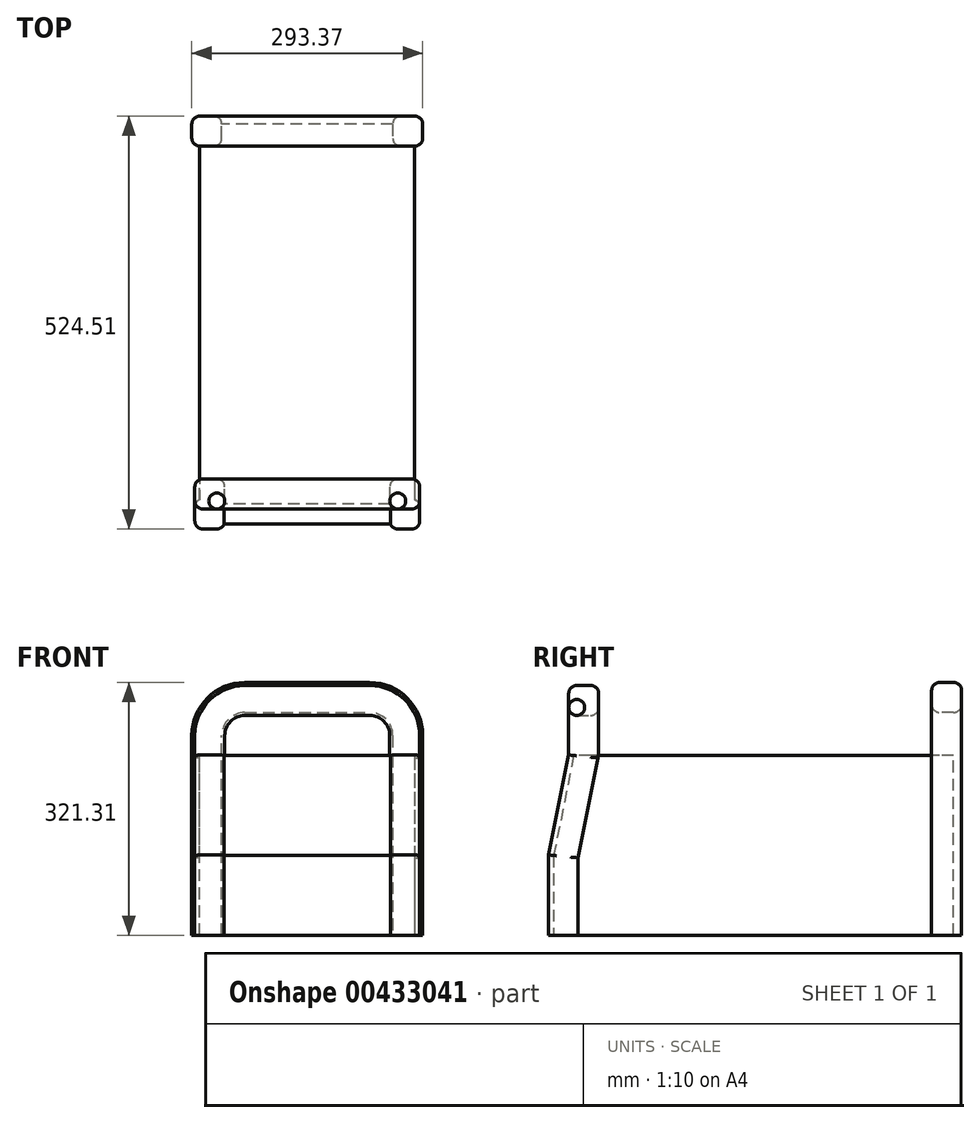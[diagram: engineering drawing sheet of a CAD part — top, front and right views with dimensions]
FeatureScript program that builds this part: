
annotation { "Feature Type Name" : "Feature", "Feature Type Description" : "" }
export const myFeature = defineFeature(function(context is Context, id is Id, definition is map)
    precondition{}
    {
        {
            var Q0;
            Q0=qCreatedBy(makeId("Right.planeOp"),FACE);
            var sketch = newSketch(context, id + "F0", { "sketchPlane" : qUnion([Q0])});
            skLineSegment(sketch, "E0", {"start": v(0, 0) * mm, "end": v(-508, 0) * mm});
            skLineSegment(sketch, "E1", {"start": v(-482.6, 228.6) * mm, "end": v(0, 228.6) * mm});
            skLineSegment(sketch, "E2", {"start": v(0, 228.6) * mm, "end": v(0, 0) * mm});
            skLineSegment(sketch, "E3", {"start": v(-482.6, 228.6) * mm, "end": v(-508, 101.6) * mm});
            skLineSegment(sketch, "E4", {"start": v(-508, 101.6) * mm, "end": v(-508, 0) * mm});
            skSolve(sketch);
        }
        {
            var Q0;
            Q0=makeQuery(id+"F0.imprint","IMPRINT",FACE,{"disambiguationData":[TD([[makeQuery(id+"F0.imprint","IMPRINT",EDGE,{"derivedFrom":sQuery(id+"F0.wireOp",EDGE,"E0")}),-1.0]])]});
            extrude(context, id + "F1", {"entities" : qUnion([Q0]), "depth" : 273.05 * mm});
        }
        {
            var Q0;
            Q0=qCreatedBy(makeId("Top.planeOp"),FACE);
            var sketch = newSketch(context, id + "F2", { "sketchPlane" : qUnion([Q0])});
            skLineSegment(sketch, "E5.bottom", {"start": v(0, 10.16) * mm, "end": v(17.78, 10.16) * mm});
            skLineSegment(sketch, "E5.top", {"start": v(0, -27.94) * mm, "end": v(17.78, -27.94) * mm});
            skLineSegment(sketch, "E5.left", {"start": v(-10.16, 0) * mm, "end": v(-10.16, -17.78) * mm});
            skLineSegment(sketch, "E5.right", {"start": v(27.94, 0) * mm, "end": v(27.94, -17.78) * mm});
            skPoint(sketch, "E6.visualSharp", {"position": v(-10.16, -27.94) * mm});
            skArc(sketch, "E6.filletArc", {"start": v(-10.16, -17.78) * mm, "mid": v(-7.18, -24.96) * mm, "end": v(0, -27.94) * mm});
            skPoint(sketch, "E7.visualSharp", {"position": v(-10.16, 10.16) * mm});
            skArc(sketch, "E7.filletArc", {"start": v(0, 10.16) * mm, "mid": v(-7.18, 7.18) * mm, "end": v(-10.16, 0) * mm});
            skPoint(sketch, "E8.visualSharp", {"position": v(27.94, 10.16) * mm});
            skArc(sketch, "E8.filletArc", {"start": v(27.94, 0) * mm, "mid": v(24.96, 7.18) * mm, "end": v(17.78, 10.16) * mm});
            skPoint(sketch, "E9.visualSharp", {"position": v(27.94, -27.94) * mm});
            skArc(sketch, "E9.filletArc", {"start": v(17.78, -27.94) * mm, "mid": v(24.96, -24.96) * mm, "end": v(27.94, -17.78) * mm});
            skSolve(sketch);
        }
        {
            var Q0;
            Q0=qCreatedBy(makeId("Front.planeOp"),FACE);
            var sketch = newSketch(context, id + "F3", { "sketchPlane" : qUnion([Q0])});
            skLineSegment(sketch, "E10", {"start": v(0, 0) * mm, "end": v(0, 254) * mm});
            skLineSegment(sketch, "E11", {"start": v(57.15, 311.15) * mm, "end": v(215.9, 311.15) * mm});
            skLineSegment(sketch, "E12", {"start": v(273.05, 254) * mm, "end": v(273.05, 0) * mm});
            skPoint(sketch, "E13.visualSharp", {"position": v(0, 311.15) * mm});
            skArc(sketch, "E13.filletArc", {"start": v(57.15, 311.15) * mm, "mid": v(16.74, 294.41) * mm, "end": v(0, 254) * mm});
            skPoint(sketch, "E14.visualSharp", {"position": v(273.05, 311.15) * mm});
            skArc(sketch, "E14.filletArc", {"start": v(273.05, 254) * mm, "mid": v(256.31, 294.41) * mm, "end": v(215.9, 311.15) * mm});
            skSolve(sketch);
        }
        {
            var Q0;
            Q0=makeQuery(id+"F2.imprint","IMPRINT",FACE,{"disambiguationData":[TD([[makeQuery(id+"F2.imprint","IMPRINT",EDGE,{"derivedFrom":sQuery(id+"F2.wireOp",EDGE,"E5.bottom")}),-1.0]])]});
            var Q1;
            Q1=sQuery(id+"F3.wireOp",EDGE,"E10");
            var Q2;
            Q2=sQuery(id+"F3.wireOp",EDGE,"E13.filletArc");
            var Q3;
            Q3=sQuery(id+"F3.wireOp",EDGE,"E11");
            var Q4;
            Q4=sQuery(id+"F3.wireOp",EDGE,"E14.filletArc");
            var Q5;
            Q5=sQuery(id+"F3.wireOp",EDGE,"E12");
            sweep(context, id + "F4", {"operationType" : NewBodyOperationType.ADD, "profiles" : qUnion([Q0]), "path" : qUnion([Q1, Q2, Q3, Q4, Q5])});
        }
        {
            var Q0;
            Q0=qCreatedBy(makeId("Top.planeOp"),FACE);
            var sketch = newSketch(context, id + "F5", { "sketchPlane" : qUnion([Q0])});
            skLineSegment(sketch, "E15.bottom", {"start": v(3.81, -514.35) * mm, "end": v(21.6, -514.35) * mm});
            skLineSegment(sketch, "E15.top", {"start": v(3.81, -476.25) * mm, "end": v(21.59, -476.25) * mm});
            skLineSegment(sketch, "E15.left", {"start": v(-6.35, -504.19) * mm, "end": v(-6.35, -486.4) * mm});
            skLineSegment(sketch, "E15.right", {"start": v(31.75, -504.19) * mm, "end": v(31.75, -486.4) * mm});
            skPoint(sketch, "E16.visualSharp", {"position": v(-6.35, -514.35) * mm});
            skArc(sketch, "E16.filletArc", {"start": v(-6.35, -504.19) * mm, "mid": v(-3.37, -511.37) * mm, "end": v(3.81, -514.35) * mm});
            skPoint(sketch, "E17.visualSharp", {"position": v(31.75, -514.35) * mm});
            skArc(sketch, "E17.filletArc", {"start": v(21.6, -514.35) * mm, "mid": v(28.77, -511.37) * mm, "end": v(31.75, -504.19) * mm});
            skPoint(sketch, "E18.visualSharp", {"position": v(31.75, -476.25) * mm});
            skArc(sketch, "E18.filletArc", {"start": v(31.75, -486.4) * mm, "mid": v(28.77, -479.23) * mm, "end": v(21.59, -476.25) * mm});
            skPoint(sketch, "E19.visualSharp", {"position": v(-6.35, -476.25) * mm});
            skArc(sketch, "E19.filletArc", {"start": v(3.8, -476.25) * mm, "mid": v(-3.37, -479.23) * mm, "end": v(-6.35, -486.4) * mm});
            skSolve(sketch);
        }
        {
            var Q0;
            Q0=makeQuery(id+"F1.opExtrude","SWEPT_FACE",FACE,{"disambiguationData":[OSD([sQuery(id+"F0.wireOp",EDGE,"E4")])]});
            cPlane(context, id + "F6", {"entities" : qUnion([Q0]), "cplaneType" : CPlaneType.OFFSET, "offset" : 25.4 * mm, "oppositeDirection" : true, "width" : 152.4 * mm, "height" : 152.4 * mm});
        }
        {
            var Q0;
            Q0=qCreatedBy(id+"F6.planeOp",FACE);
            var sketch = newSketch(context, id + "F7", { "sketchPlane" : qUnion([Q0])});
            skLineSegment(sketch, "E20", {"start": v(0, 228.6) * mm, "end": v(0, 254) * mm});
            skLineSegment(sketch, "E21", {"start": v(57.15, 311.15) * mm, "end": v(215.9, 311.15) * mm});
            skLineSegment(sketch, "E22", {"start": v(273.05, 254) * mm, "end": v(273.05, 228.6) * mm});
            skPoint(sketch, "E23.visualSharp", {"position": v(0, 311.15) * mm});
            skArc(sketch, "E23.filletArc", {"start": v(57.15, 311.15) * mm, "mid": v(16.74, 294.41) * mm, "end": v(0, 254) * mm});
            skPoint(sketch, "E24.visualSharp", {"position": v(273.05, 311.15) * mm});
            skArc(sketch, "E24.filletArc", {"start": v(273.05, 254) * mm, "mid": v(256.31, 294.41) * mm, "end": v(215.9, 311.15) * mm});
            skSolve(sketch);
        }
        {
            var Q0;
            Q0=makeQuery(id+"F5.imprint","IMPRINT",FACE,{"disambiguationData":[TD([[makeQuery(id+"F5.imprint","IMPRINT",EDGE,{"derivedFrom":sQuery(id+"F5.wireOp",EDGE,"E15.bottom")}),1.0]])]});
            var Q1;
            Q1=makeQuery(id+"F1.opExtrude","CAP_EDGE",EDGE,{"disambiguationData":[OSD([sQuery(id+"F0.wireOp",EDGE,"E4")])],"isStart":true});
            var Q2;
            Q2=makeQuery(id+"F1.opExtrude","CAP_EDGE",EDGE,{"disambiguationData":[OSD([sQuery(id+"F0.wireOp",EDGE,"E3")])],"isStart":true});
            var Q3;
            Q3=sQuery(id+"F7.wireOp",EDGE,"E20");
            var Q4;
            Q4=sQuery(id+"F7.wireOp",EDGE,"E23.filletArc");
            var Q5;
            Q5=sQuery(id+"F7.wireOp",EDGE,"E21");
            var Q6;
            Q6=sQuery(id+"F7.wireOp",EDGE,"E24.filletArc");
            var Q7;
            Q7=sQuery(id+"F7.wireOp",EDGE,"E22");
            var Q8;
            Q8=makeQuery(id+"F1.opExtrude","CAP_EDGE",EDGE,{"disambiguationData":[OSD([sQuery(id+"F0.wireOp",EDGE,"E3")])],"isStart":false});
            var Q9;
            Q9=makeQuery(id+"F1.opExtrude","CAP_EDGE",EDGE,{"disambiguationData":[OSD([sQuery(id+"F0.wireOp",EDGE,"E4")])],"isStart":false});
            sweep(context, id + "F8", {"operationType" : NewBodyOperationType.ADD, "profiles" : qUnion([Q0]), "path" : qUnion([Q1, Q2, Q3, Q4, Q5, Q6, Q7, Q8, Q9])});
        }
    });
